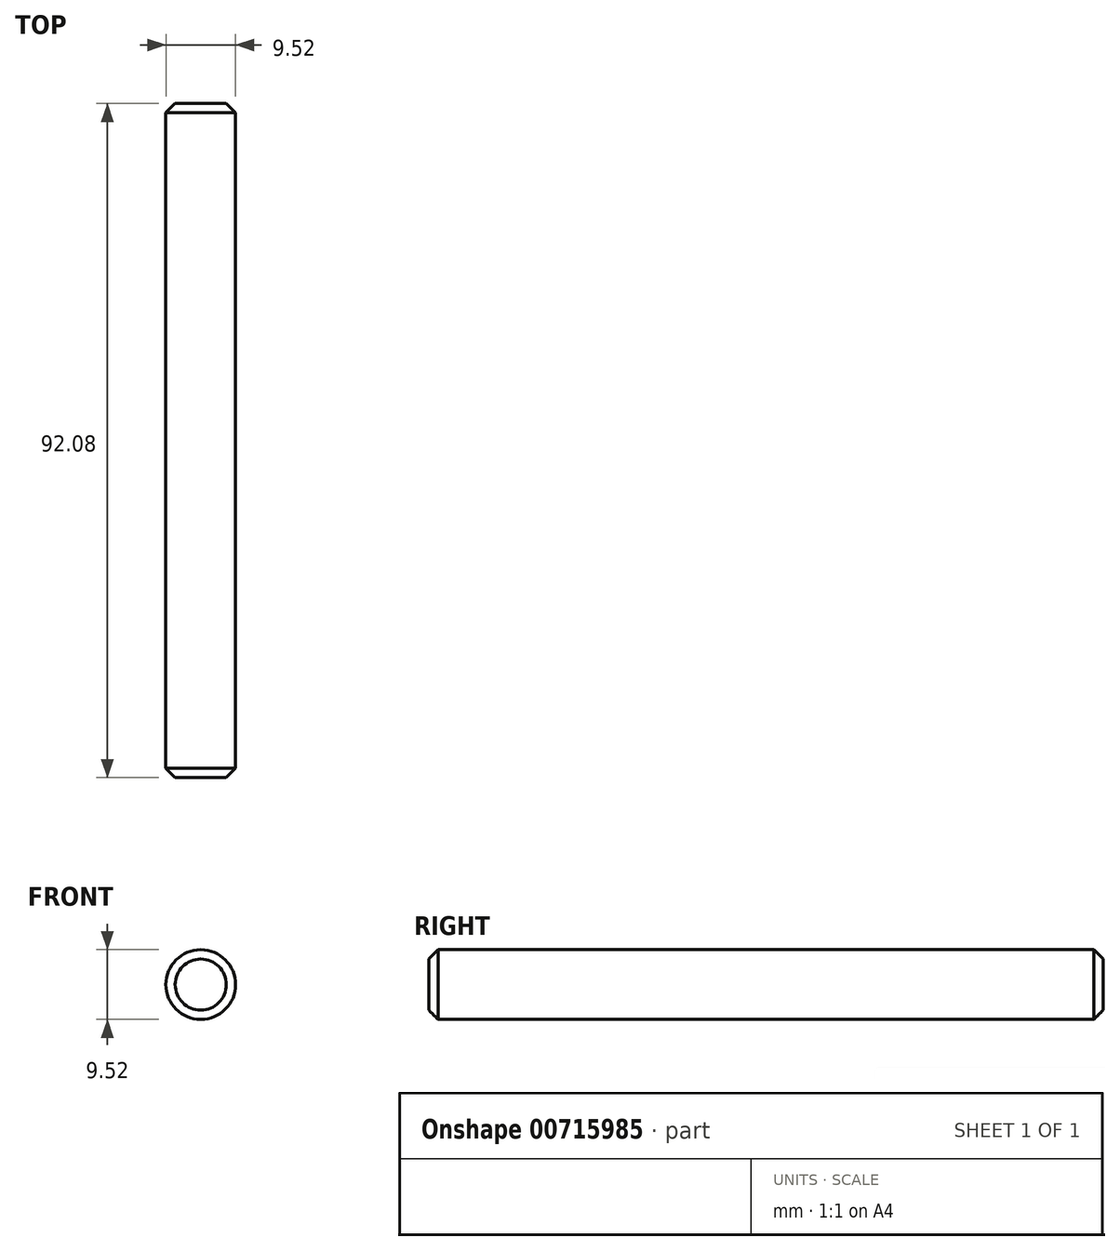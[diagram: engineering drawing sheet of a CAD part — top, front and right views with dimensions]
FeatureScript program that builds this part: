
annotation { "Feature Type Name" : "Feature", "Feature Type Description" : "" }
export const myFeature = defineFeature(function(context is Context, id is Id, definition is map)
    precondition{}
    {
        {
            var Q0;
            Q0=qCreatedBy(makeId("Front.planeOp"),FACE);
            var sketch = newSketch(context, id + "F0", { "sketchPlane" : qUnion([Q0])});
            skCircle(sketch, "E0", {"center": v(0, 0) * mm, "radius": 4.76 * mm});
            skSolve(sketch);
        }
        {
            var Q0;
            Q0 = qSketchRegion(id + "F0", true);
            var Q1;
            Q1=makeQuery(id+"F0.imprint","IMPRINT",FACE,{"disambiguationData":[TD([[makeQuery(id+"F0.imprint","IMPRINT",EDGE,{"derivedFrom":sQuery(id+"F0.wireOp",EDGE,"E0")}),1.0]])]});
            extrude(context, id + "F1", {"entities" : qUnion([Q0, Q1]), "oppositeDirection" : true, "depth" : 92.07 * mm, "offsetDistance" : 25.4 * mm});
        }
        {
            var Q0;
            Q0=makeQuery(id+"F1.opExtrude","CAP_EDGE",EDGE,{"disambiguationData":[OSD([sQuery(id+"F0.wireOp",EDGE,"E0")])],"isStart":true});
            var Q1;
            Q1=makeQuery(id+"F1.opExtrude","CAP_EDGE",EDGE,{"disambiguationData":[OSD([sQuery(id+"F0.wireOp",EDGE,"E0")])],"isStart":false});
            chamfer(context, id + "F2", {"entities" : qUnion([Q0, Q1]), "width" : 1.27 * mm, "tangentPropagation" : true});
        }
    });
